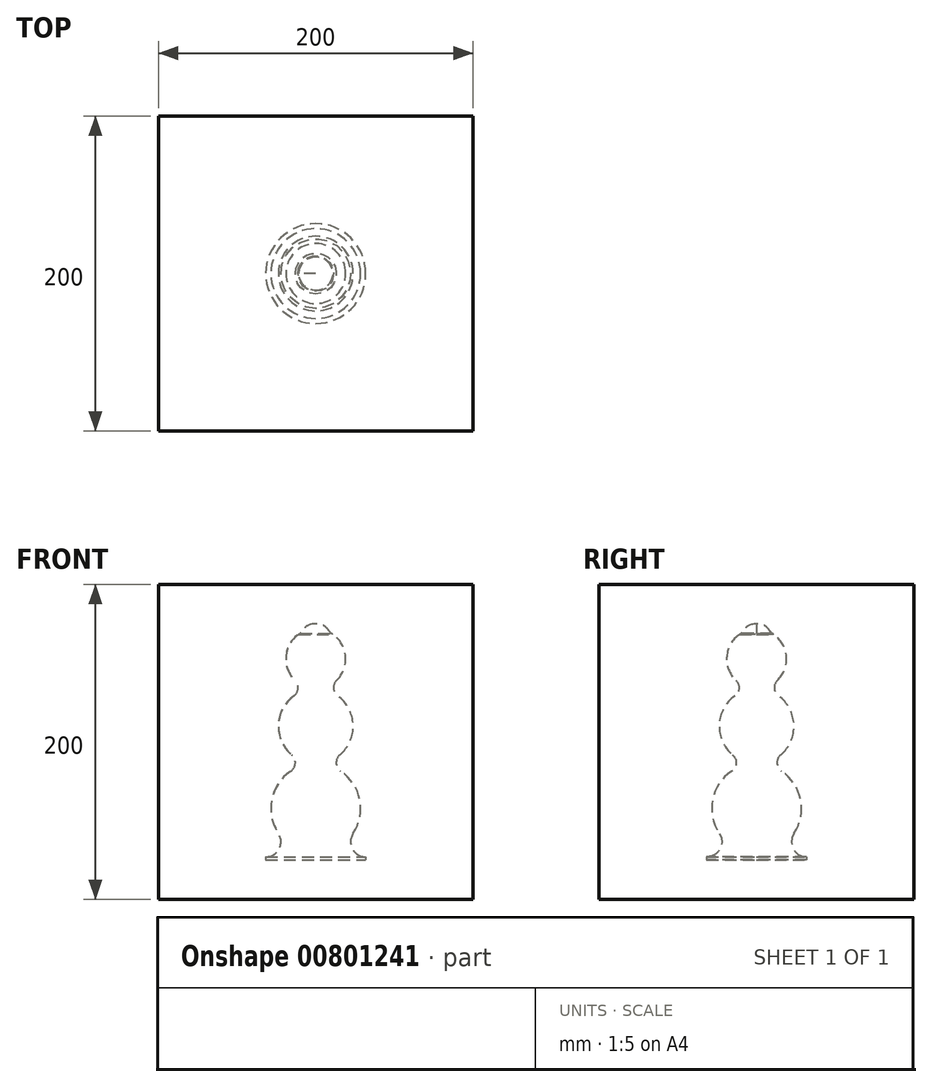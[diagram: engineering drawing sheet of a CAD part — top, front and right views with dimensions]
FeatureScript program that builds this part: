
annotation { "Feature Type Name" : "Feature", "Feature Type Description" : "" }
export const myFeature = defineFeature(function(context is Context, id is Id, definition is map)
    precondition{}
    {
        {
            var Q0;
            Q0=qCreatedBy(makeId("Front.planeOp"),FACE);
            var sketch = newSketch(context, id + "F0", { "sketchPlane" : qUnion([Q0])});
            skLineSegment(sketch, "E0.bottom", {"start": v(-100, 100) * mm, "end": v(100, 100) * mm});
            skLineSegment(sketch, "E0.top", {"start": v(-100, -100) * mm, "end": v(100, -100) * mm});
            skLineSegment(sketch, "E0.left", {"start": v(-100, 100) * mm, "end": v(-100, -100) * mm});
            skLineSegment(sketch, "E0.right", {"start": v(100, 100) * mm, "end": v(100, -100) * mm});
            skLineSegment(sketch, "E1", {"start": v(0, 0) * mm, "end": v(100, 0) * mm, "construction": true});
            skSolve(sketch);
        }
        {
            var Q0;
            Q0=makeQuery(id+"F0.imprint","IMPRINT",FACE,{"disambiguationData":[TD([[makeQuery(id+"F0.imprint","IMPRINT",EDGE,{"derivedFrom":sQuery(id+"F0.wireOp",EDGE,"E0.bottom")}),-1.0]])]});
            extrude(context, id + "F1", {"entities" : qUnion([Q0]), "endBound" : BoundingType.SYMMETRIC, "depth" : 200 * mm, "offsetDistance" : 25 * mm});
        }
        {
            var Q0;
            Q0=qCreatedBy(makeId("Front.planeOp"),FACE);
            var sketch = newSketch(context, id + "F2", { "sketchPlane" : qUnion([Q0])});
            skLineSegment(sketch, "E2", {"start": v(0, -75) * mm, "end": v(0, 75) * mm});
            skLineSegment(sketch, "E3", {"start": v(0, -75) * mm, "end": v(-31.75, -75) * mm});
            skCircle(sketch, "E4", {"center": v(0, 52.7) * mm, "radius": 19 * mm});
            skCircle(sketch, "E5", {"center": v(0, 9.95) * mm, "radius": 23.75 * mm});
            skCircle(sketch, "E6", {"center": v(0, -42.3) * mm, "radius": 28.5 * mm});
            skLineSegment(sketch, "E7", {"start": v(-28.5, -42.3) * mm, "end": v(28.5, -42.3) * mm, "construction": true});
            skLineSegment(sketch, "E8", {"start": v(-23.75, 9.95) * mm, "end": v(23.75, 9.95) * mm, "construction": true});
            skLineSegment(sketch, "E9", {"start": v(-19, 52.7) * mm, "end": v(19, 52.7) * mm, "construction": true});
            skFitSpline(sketch, "E10", {"points": [v(0, 75) * mm, v(-10.74, 68.38) * mm], "startDerivative": vector(-23.41, 0) * mm, "endDerivative": vector(-10.8, -5.8) * mm});
            skLineSegment(sketch, "E11", {"start": v(-7.8, 75) * mm, "end": v(7.8, 75) * mm, "construction": true});
            skCircle(sketch, "E12", {"center": v(-17.65, 34.41) * mm, "radius": 6.41 * mm});
            skCircle(sketch, "E13", {"center": v(-19.51, -13.2) * mm, "radius": 6.53 * mm});
            skPoint(sketch, "E14", {"position": v(0, 33.7) * mm});
            skPoint(sketch, "E15", {"position": v(0, -13.8) * mm});
            skLineSegment(sketch, "E16", {"start": v(-31.75, -75) * mm, "end": v(-31.75, -73) * mm});
            skLineSegment(sketch, "E17", {"start": v(-31.75, -73) * mm, "end": v(-31.75, -63.39) * mm, "construction": true});
            skArc(sketch, "E18", {"start": v(-31.75, -73) * mm, "mid": v(-23.28, -67.93) * mm, "end": v(-23.74, -58.07) * mm});
            skSolve(sketch);
        }
        {
            var Q0;
            {var subQ0=sQuery(id+"F2.wireOp",EDGE,"E10");var subQ1=sQuery(id+"F2.wireOp",EDGE,"E2");var subQ2=makeQuery(id+"F2.imprint","INTERSECT",VERTEX,{"derivedFrom":[subQ1,subQ0]});Q0=makeQuery(id+"F2.imprint","IMPRINT",FACE,{"disambiguationData":[TD([[makeQuery(id+"F2.imprint","IMPRINT",EDGE,{"disambiguationData":[TD([[subQ2,1.0]])],"derivedFrom":subQ1}),1.0]])]});}
            var Q1;
            {var subQ0=sQuery(id+"F2.wireOp",EDGE,"E4");var subQ2=sQuery(id+"F2.wireOp",EDGE,"E2");var subQ7=makeQuery(id+"F2.imprint","INTERSECT",VERTEX,{"derivedFrom":[subQ2,subQ0]});Q1=makeQuery(id+"F2.imprint","IMPRINT",FACE,{"disambiguationData":[TD([[makeQuery(id+"F2.imprint","IMPRINT",EDGE,{"disambiguationData":[TD([[subQ7,-1.0]])],"derivedFrom":subQ0}),1.0]])]});}
            var Q2;
            {var subQ0=sQuery(id+"F2.wireOp",EDGE,"E12");var subQ1=sQuery(id+"F2.wireOp",EDGE,"E4");var subQ2=makeQuery(id+"F2.imprint","INTERSECT",VERTEX,{"derivedFrom":[subQ1,subQ0]});Q2=makeQuery(id+"F2.imprint","IMPRINT",FACE,{"disambiguationData":[TD([[makeQuery(id+"F2.imprint","IMPRINT",EDGE,{"disambiguationData":[TD([[subQ2,1.0]])],"derivedFrom":subQ0}),-1.0]])]});}
            var Q3;
            {var subQ0=sQuery(id+"F2.wireOp",EDGE,"E5");var subQ4=makeQuery(id+"F2.imprint","INTERSECT",VERTEX,{"derivedFrom":[subQ0,sQuery(id+"F2.wireOp",EDGE,"E12")]});Q3=makeQuery(id+"F2.imprint","IMPRINT",FACE,{"disambiguationData":[TD([[makeQuery(id+"F2.imprint","IMPRINT",EDGE,{"disambiguationData":[TD([[subQ4,-1.0]])],"derivedFrom":subQ0}),1.0]])]});}
            var Q4;
            {var subQ0=sQuery(id+"F2.wireOp",EDGE,"E13");var subQ1=sQuery(id+"F2.wireOp",EDGE,"E5");var subQ2=makeQuery(id+"F2.imprint","INTERSECT",VERTEX,{"derivedFrom":[subQ1,subQ0]});Q4=makeQuery(id+"F2.imprint","IMPRINT",FACE,{"disambiguationData":[TD([[makeQuery(id+"F2.imprint","IMPRINT",EDGE,{"disambiguationData":[TD([[subQ2,1.0]])],"derivedFrom":subQ0}),-1.0]])]});}
            var Q5;
            {var subQ0=sQuery(id+"F2.wireOp",EDGE,"E6");var subQ4=makeQuery(id+"F2.imprint","INTERSECT",VERTEX,{"derivedFrom":[subQ0,sQuery(id+"F2.wireOp",EDGE,"E18")]});Q5=makeQuery(id+"F2.imprint","IMPRINT",FACE,{"disambiguationData":[TD([[makeQuery(id+"F2.imprint","IMPRINT",EDGE,{"disambiguationData":[TD([[subQ4,1.0]])],"derivedFrom":subQ0}),1.0]])]});}
            var Q6;
            {var subQ4=sQuery(id+"F2.wireOp",EDGE,"E3");Q6=makeQuery(id+"F2.imprint","IMPRINT",FACE,{"disambiguationData":[TD([[makeQuery(id+"F2.imprint","IMPRINT",EDGE,{"derivedFrom":subQ4}),-1.0]])]});}
            var Q7;
            Q7=sQuery(id+"F2.wireOp",EDGE,"E2");
            revolve(context, id + "F3", {"surfaceOperationType" : NewSurfaceOperationType.NEW, "entities" : qUnion([Q0, Q1, Q2, Q3, Q4, Q5, Q6]), "axis" : qUnion([Q7]), "revolveType" : RevolveType.FULL});
        }
    });
